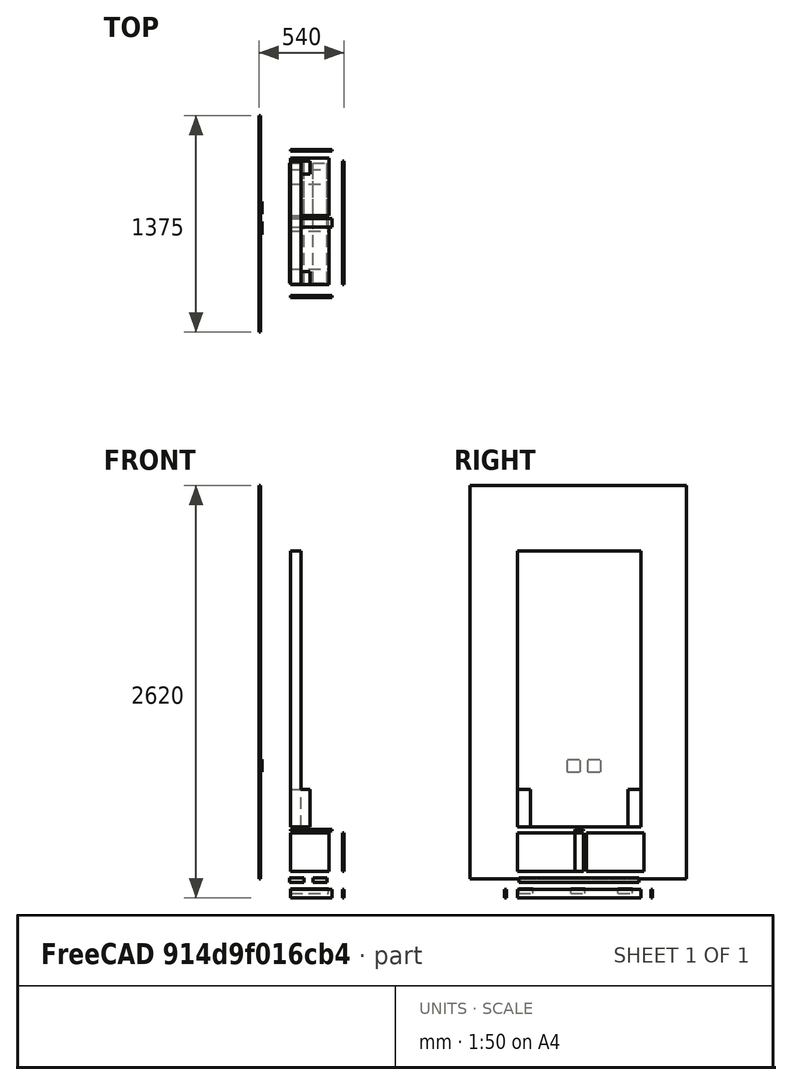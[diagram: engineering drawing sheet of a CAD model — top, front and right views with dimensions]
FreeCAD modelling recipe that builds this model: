
FCSTD DOCUMENT  (FreeCAD 0.18.4R)
Label: spiegelv5
License: All rights reserved
LicenseURL: http://en.wikipedia.org/wiki/All_rights_reserved
objects: Part::Box×19, Part::FeaturePython×2, App::Part×1, Drawing::FeaturePage×1
note: 21 computed .brp shape members not serialized (recipe doc carries the construction recipe); baked Part::Feature solids carry a one-line shape summary decoded from their .brp

FEATURE [App::Part] Part  label="Spiegel"
  Origin = -> Origin
FEATURE [Drawing::FeaturePage] Page
  EditableTexts = AUTHOR NAME | CREATION DATE | SUPERVISOR NAME | CHECK DATE | SCALE | WEIGHT | NUMBER | SHEET | TITLE | SUBTITLE
  Template = <path>
FEATURE [Part::Box] Box  label="SockelLinks"
  AttacherType = Attacher::AttachEngine3D
  Height = 241
  Length = 124.5
  Width = 83
FEATURE [Part::Box] Box001  label="SpiegelFlaecheUeberSockel"
  AttacherType = Attacher::AttachEngine3D
  Height = 1513
  Length = 65.5
  Placement = pos=(0,0,241) rot=(0,0,1;0rad)
  Width = 784
FEATURE [Part::Box] Box002  label="SockelRechts"
  AttacherType = Attacher::AttachEngine3D
  Height = 241
  Length = 124.5
  Placement = pos=(0,702,0) rot=(0,0,1;0rad)
  Width = 83
FEATURE [Part::Box] Box003  label="SpiegelFlaecheZwischenSockel"
  AttacherType = Attacher::AttachEngine3D
  Height = 241
  Length = 65.5
  Placement = pos=(0,83,0) rot=(0,0,1;0rad)
  Width = 619
FEATURE [Part::FeaturePython] Connect  # WARN: FeaturePython — macro-defined, semantics opaque (R4)
  Objects = -> [Box001,Box003]
  Tolerance = 0
FEATURE [Part::FeaturePython] Connect001  label="spiegelBody"  # WARN: FeaturePython — macro-defined, semantics opaque (R4)
  Objects = -> [Connect,Box002,Box]
  Tolerance = 0
FEATURE [Part::Box] Box004  label="BodenKonstrLeiste1"
  AttacherType = Attacher::AttachEngine3D
  Height = 27
  Length = 91
  Placement = pos=(142,10,-350) rot=(0,0,1;0rad)
  Width = 764
FEATURE [Part::Box] Box005  label="BodenKonstrLeiste002"
  AttacherType = Attacher::AttachEngine3D
  Height = 27
  Length = 91
  Placement = pos=(-6,10,-350) rot=(0,0,1;0rad)
  Width = 764
FEATURE [Part::Box] Box006  label="OHP_left"
  AttacherType = Attacher::AttachEngine3D
  Height = 244
  Length = 244
  Placement = pos=(0,0,-280) rot=(0,0,1;0rad)
  Width = 365
FEATURE [Part::Box] Box007  label="BodenKonstrFuß1"
  AttacherType = Attacher::AttachEngine3D
  Height = 27
  Length = 240
  Placement = pos=(0,10,-420) rot=(0,0,1;0rad)
  Width = 91
FEATURE [Part::Box] Box008  label="BodenKonstrFuß002"
  AttacherType = Attacher::AttachEngine3D
  Height = 27
  Length = 240
  Placement = pos=(0,340,-420) rot=(0,0,1;0rad)
  Width = 91
FEATURE [Part::Box] Box009  label="BodenKonstrFuß003"
  AttacherType = Attacher::AttachEngine3D
  Height = 27
  Length = 240
  Placement = pos=(0,640,-420) rot=(0,0,1;0rad)
  Width = 91
FEATURE [Part::Box] Box010  label="OHP_right"
  AttacherType = Attacher::AttachEngine3D
  Height = 244
  Length = 244
  Placement = pos=(0,440,-280) rot=(0,0,1;0rad)
  Width = 365
FEATURE [Part::Box] Box011  label="wand"
  AttacherType = Attacher::AttachEngine3D
  Height = 2500
  Length = 10
  Placement = pos=(-200,-300,-330) rot=(0,0,1;0rad)
  Width = 1375
FEATURE [Part::Box] Box012  label="Steckdose1"
  AttacherType = Attacher::AttachEngine3D
  Height = 80
  Length = 20
  Placement = pos=(-200,320,350) rot=(0,0,1;0rad)
  Width = 80
FEATURE [Part::Box] Box013  label="Steckdose2"
  AttacherType = Attacher::AttachEngine3D
  Height = 80
  Length = 20
  Placement = pos=(-200,450,350) rot=(0,0,1;0rad)
  Width = 80
FEATURE [Part::Box] Box014  label="bodenleisteLinks"
  AttacherType = Attacher::AttachEngine3D
  Height = 56
  Length = 262
  Placement = pos=(0,-80,-450) rot=(0,0,1;0rad)
  Width = 10
FEATURE [Part::Box] Box015  label="bodenleisteRechts"
  AttacherType = Attacher::AttachEngine3D
  Height = 56
  Length = 262
  Placement = pos=(0,850,-450) rot=(0,0,1;0rad)
  Width = 10
FEATURE [Part::Box] Box016  label="bodenleisteFront"
  AttacherType = Attacher::AttachEngine3D
  Height = 56
  Length = 10
  Placement = pos=(330,0,-450) rot=(0,0,1;0rad)
  Width = 785
FEATURE [Part::Box] Box018  label="mittelLeisteFron"
  AttacherType = Attacher::AttachEngine3D
  Height = 244
  Length = 10
  Placement = pos=(330,365,-280) rot=(0,0,1;0rad)
  Width = 55
FEATURE [Part::Box] Box019  label="mittelLeisteOben"
  AttacherType = Attacher::AttachEngine3D
  Height = 10
  Length = 262
  Placement = pos=(0,365,-24) rot=(0,0,1;0rad)
  Width = 55
note: 1 file-system path scrubbed to <path> (originals preserved in the JSON sidecar)
